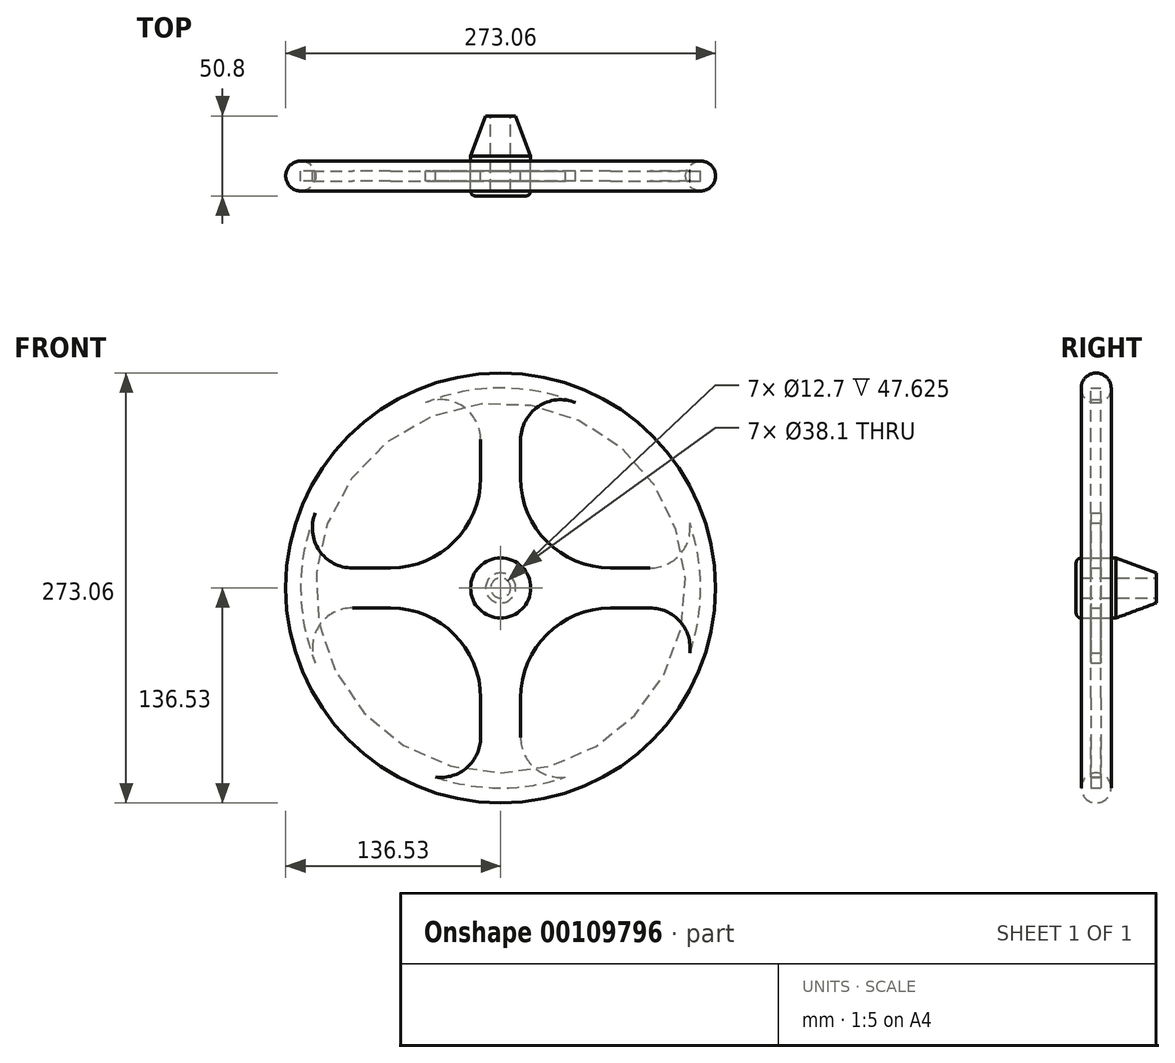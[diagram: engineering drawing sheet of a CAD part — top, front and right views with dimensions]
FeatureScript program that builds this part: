
annotation { "Feature Type Name" : "Feature", "Feature Type Description" : "" }
export const myFeature = defineFeature(function(context is Context, id is Id, definition is map)
    precondition{}
    {
        {
            var Q0;
            Q0=qCreatedBy(makeId("Front.planeOp"),FACE);
            var sketch = newSketch(context, id + "F0", { "sketchPlane" : qUnion([Q0])});
            skCircle(sketch, "E0", {"center": v(0, 0) * mm, "radius": 19.05 * mm});
            skSolve(sketch);
        }
        {
            var Q0;
            Q0=qCreatedBy(makeId("Right.planeOp"),FACE);
            var sketch = newSketch(context, id + "F1", { "sketchPlane" : qUnion([Q0])});
            skCircle(sketch, "E1", {"center": v(0, 127) * mm, "radius": 9.53 * mm});
            skSolve(sketch);
        }
        {
            var Q0;
            Q0=makeQuery(id+"F1.imprint","IMPRINT",FACE,{"disambiguationData":[TD([[makeQuery(id+"F1.imprint","IMPRINT",EDGE,{"derivedFrom":sQuery(id+"F1.wireOp",EDGE,"E1")}),1.0]])]});
            var Q1;
            Q1=sQuery(id+"F0.wireOp",EDGE,"E0");
            sweep(context, id + "F2", {"profiles" : qUnion([Q0]), "path" : qUnion([Q1])});
        }
        {
            var Q0;
            Q0 = qSketchRegion(id + "F0", true);
            extrude(context, id + "F3", {"entities" : qUnion([Q0]), "depth" : 12.7 * mm, "hasSecondDirection" : true, "secondDirectionOppositeDirection" : true, "secondDirectionDepth" : 38.1 * mm});
        }
        {
            var Q0;
            Q0=makeQuery(id+"F3.opExtrude","CAP_EDGE",EDGE,{"disambiguationData":[OSD([sQuery(id+"F0.wireOp",EDGE,"E0")])],"isStart":true});
            chamfer(context, id + "F4", {"entities" : qUnion([Q0]), "chamferType" : ChamferType.TWO_OFFSETS, "width1" : 25.4 * mm, "oppositeDirection" : false, "width2" : 9.52 * mm, "tangentPropagation" : true});
        }
        {
            var Q0;
            Q0=makeQuery(id+"F3.opExtrude","CAP_FACE",FACE,{"disambiguationData":[OSD([sQuery(id+"F0.wireOp",EDGE,"E0")])],"isStart":true});
            var sketch = newSketch(context, id + "F5", { "sketchPlane" : qUnion([Q0])});
            skCircle(sketch, "E2", {"center": v(0, 0) * mm, "radius": 6.35 * mm});
            skSolve(sketch);
        }
        {
            var Q0;
            Q0=makeQuery(id+"F3.opExtrude","CAP_EDGE",EDGE,{"disambiguationData":[OSD([sQuery(id+"F0.wireOp",EDGE,"E0")])],"isStart":false});
            fillet(context, id + "F6", {"entities" : qUnion([Q0]), "radius" : 3.16 * mm, "tangentPropagation" : true, "allowEdgeOverflow" : false});
        }
        {
            var Q0;
            Q0 = qSketchRegion(id + "F5", true);
            extrude(context, id + "F7", {"entities" : qUnion([Q0]), "operationType" : NewBodyOperationType.REMOVE, "oppositeDirection" : true, "depth" : 47.62 * mm});
        }
        {
            var Q0;
            Q0=qCreatedBy(makeId("Front.planeOp"),FACE);
            var sketch = newSketch(context, id + "F8", { "sketchPlane" : qUnion([Q0])});
            skArc(sketch, "E3", {"start": v(-69.85, 12.7) * mm, "mid": v(-29.44, 29.44) * mm, "end": v(-12.7, 69.85) * mm});
            skArc(sketch, "E4", {"start": v(12.7, 69.85) * mm, "mid": v(29.44, 29.44) * mm, "end": v(69.85, 12.7) * mm});
            skArc(sketch, "E5", {"start": v(-12.7, -69.85) * mm, "mid": v(-29.44, -29.44) * mm, "end": v(-69.85, -12.7) * mm});
            skArc(sketch, "E6", {"start": v(69.85, -12.7) * mm, "mid": v(29.44, -29.44) * mm, "end": v(12.7, -69.85) * mm});
            skArc(sketch, "E7", {"start": v(47.62, 117.73) * mm, "mid": v(17.99, 125.72) * mm, "end": v(-12.7, 126.36) * mm});
            skCircle(sketch, "E8", {"center": v(0, 0) * mm, "radius": 19.05 * mm});
            skLineSegment(sketch, "E9", {"start": v(-12.7, 69.85) * mm, "end": v(-12.7, 126.36) * mm});
            skLineSegment(sketch, "E10.MirrorCS", {"start": v(12.7, 69.85) * mm, "end": v(12.7, 94.19) * mm});
            skLineSegment(sketch, "E11.MirrorCS", {"start": v(-12.7, -69.85) * mm, "end": v(-12.7, -94.92) * mm});
            skLineSegment(sketch, "E12.MirrorCS", {"start": v(12.7, -69.85) * mm, "end": v(12.7, -94.92) * mm});
            skLineSegment(sketch, "E13", {"start": v(-69.85, 12.7) * mm, "end": v(-94.19, 12.7) * mm});
            skLineSegment(sketch, "E14.MirrorCS", {"start": v(-69.85, -12.7) * mm, "end": v(-94.19, -12.7) * mm});
            skLineSegment(sketch, "E15.MirrorCS", {"start": v(69.85, 12.7) * mm, "end": v(94.92, 12.7) * mm});
            skLineSegment(sketch, "E16.MirrorCS", {"start": v(69.85, -12.7) * mm, "end": v(94.92, -12.7) * mm});
            skPoint(sketch, "E17.newPointA", {"position": v(12.7, 126.36) * mm});
            skArc(sketch, "E17.filletArc", {"start": v(47.62, 117.73) * mm, "mid": v(23.9, 115.25) * mm, "end": v(12.7, 94.19) * mm});
            skPoint(sketch, "E18.newPointA", {"position": v(126.36, 12.7) * mm});
            skArc(sketch, "E18.filletArc", {"start": v(94.92, 12.7) * mm, "mid": v(113.95, 21.27) * mm, "end": v(120.14, 41.19) * mm});
            skPoint(sketch, "E19.newPointA", {"position": v(-12.7, -126.36) * mm});
            skArc(sketch, "E19.filletArc", {"start": v(-41.19, -120.14) * mm, "mid": v(-21.27, -113.95) * mm, "end": v(-12.7, -94.92) * mm});
            skPoint(sketch, "E20.newPointA", {"position": v(-126.36, -12.7) * mm});
            skArc(sketch, "E20.filletArc", {"start": v(-94.19, -12.7) * mm, "mid": v(-115.25, -23.9) * mm, "end": v(-117.73, -47.62) * mm});
            skArc(sketch, "E21.MirrorCS", {"start": v(-47.62, 117.73) * mm, "mid": v(-23.9, 115.25) * mm, "end": v(-12.7, 94.19) * mm});
            skArc(sketch, "E22.MirrorCS", {"start": v(41.19, -120.14) * mm, "mid": v(21.27, -113.95) * mm, "end": v(12.7, -94.92) * mm});
            skArc(sketch, "E23.MirrorCS", {"start": v(-94.19, 12.7) * mm, "mid": v(-115.25, 23.9) * mm, "end": v(-117.73, 47.62) * mm});
            skArc(sketch, "E24.MirrorCS", {"start": v(94.92, -12.7) * mm, "mid": v(113.95, -21.27) * mm, "end": v(120.14, -41.19) * mm});
            skPoint(sketch, "E25.orphan", {"position": v(126.36, -12.7) * mm});
            skPoint(sketch, "E26.orphan", {"position": v(12.7, -126.36) * mm});
            skPoint(sketch, "E27.orphan", {"position": v(-126.36, 12.7) * mm});
            skArc(sketch, "E28.converted", {"start": v(-117.73, 47.62) * mm, "mid": v(-127, 0) * mm, "end": v(-117.73, -47.62) * mm});
            skArc(sketch, "E29.trimOffspring", {"start": v(47.62, 117.73) * mm, "mid": v(0, 127) * mm, "end": v(-47.62, 117.73) * mm});
            skArc(sketch, "E30.trimOffspring", {"start": v(120.14, -41.19) * mm, "mid": v(127, 0) * mm, "end": v(120.14, 41.19) * mm});
            skArc(sketch, "E31.trimOffspring", {"start": v(-41.19, -120.14) * mm, "mid": v(0, -127) * mm, "end": v(41.19, -120.14) * mm});
            skSolve(sketch);
        }
        {
            var Q0;
            Q0 = qSketchRegion(id + "F8", true);
            extrude(context, id + "F9", {"entities" : qUnion([Q0]), "endBound" : BoundingType.SYMMETRIC, "depth" : 6.35 * mm});
        }
    });
